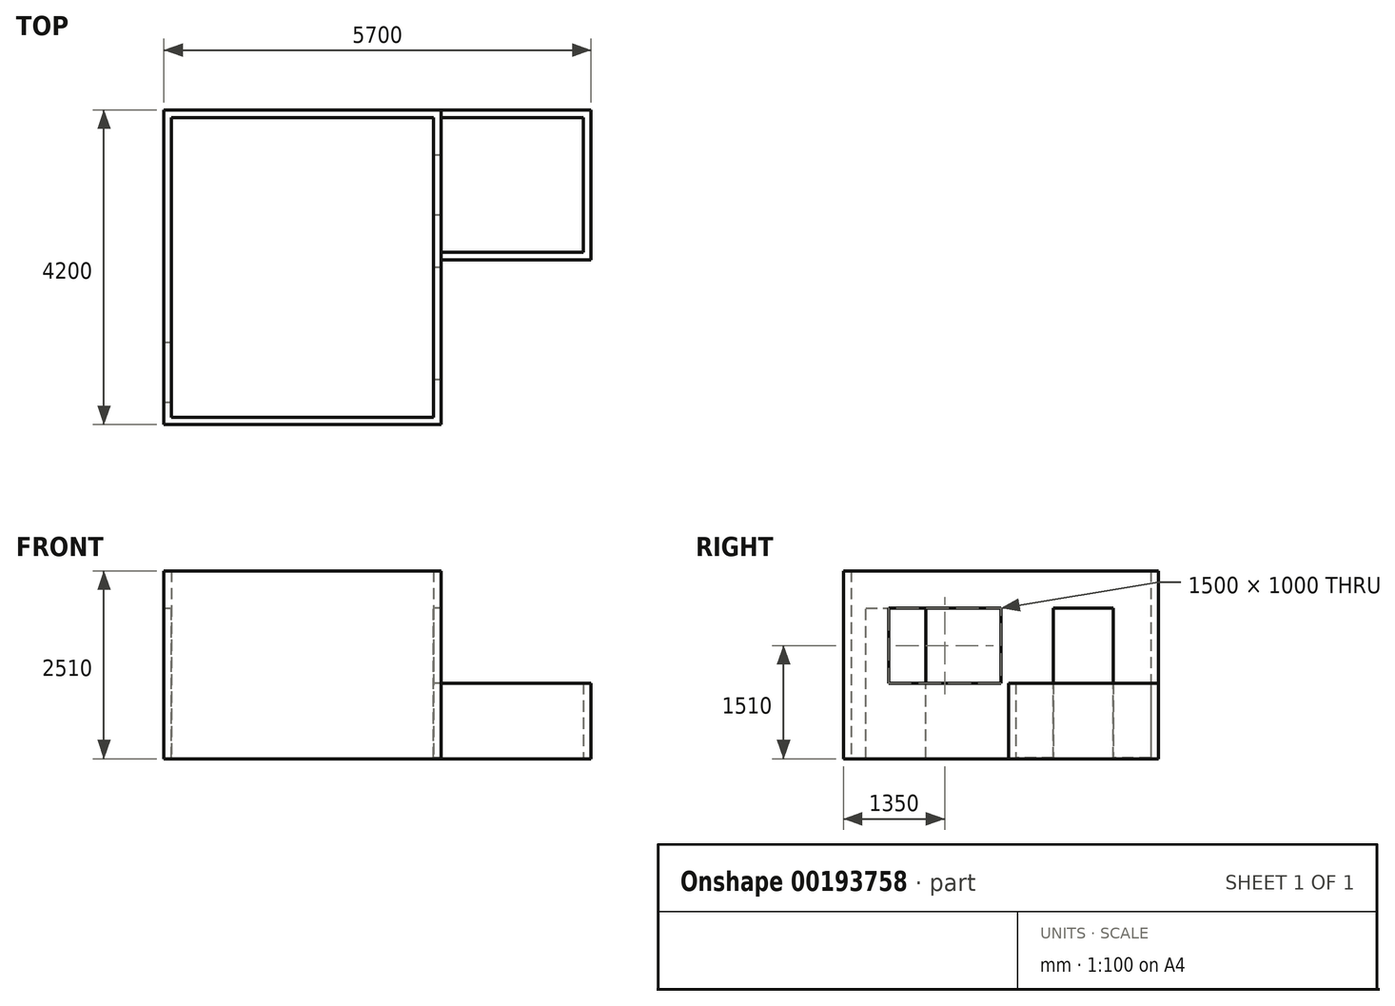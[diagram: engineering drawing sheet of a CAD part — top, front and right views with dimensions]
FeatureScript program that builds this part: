
annotation { "Feature Type Name" : "Feature", "Feature Type Description" : "" }
export const myFeature = defineFeature(function(context is Context, id is Id, definition is map)
    precondition{}
    {
        {
            var Q0;
            Q0=qCreatedBy(makeId("Top.planeOp"),FACE);
            var sketch = newSketch(context, id + "F0", { "sketchPlane" : qUnion([Q0])});
            skLineSegment(sketch, "E0.bottom", {"start": v(0, 0) * mm, "end": v(3500, 0) * mm, "construction": true});
            skLineSegment(sketch, "E0.top", {"start": v(0, 4000) * mm, "end": v(3500, 4000) * mm, "construction": true});
            skLineSegment(sketch, "E0.left", {"start": v(0, 0) * mm, "end": v(0, 4000) * mm, "construction": true});
            skLineSegment(sketch, "E0.right", {"start": v(3500, 0) * mm, "end": v(3500, 4000) * mm, "construction": true});
            skLineSegment(sketch, "E1.bottom", {"start": v(-100, 4100) * mm, "end": v(3600, 4100) * mm});
            skLineSegment(sketch, "E1.top", {"start": v(-100, -100) * mm, "end": v(3600, -100) * mm});
            skLineSegment(sketch, "E1.left", {"start": v(-100, 4100) * mm, "end": v(-100, -100) * mm});
            skLineSegment(sketch, "E1.right", {"start": v(3600, 4100) * mm, "end": v(3600, -100) * mm});
            skSolve(sketch);
        }
        {
            var Q0;
            Q0=makeQuery(id+"F0.imprint","IMPRINT",FACE,{"disambiguationData":[TD([[makeQuery(id+"F0.imprint","IMPRINT",EDGE,{"derivedFrom":sQuery(id+"F0.wireOp",EDGE,"E1.bottom")}),-1.0]])]});
            extrude(context, id + "F1", {"entities" : qUnion([Q0]), "oppositeDirection" : true, "depth" : 10 * mm});
        }
        {
            var Q0;
            Q0=makeQuery(id+"F0.imprint","IMPRINT",FACE,{"disambiguationData":[TD([[makeQuery(id+"F0.imprint","IMPRINT",EDGE,{"derivedFrom":sQuery(id+"F0.wireOp",EDGE,"E1.bottom")}),-1.0]])]});
            var sketch = newSketch(context, id + "F2", { "sketchPlane" : qUnion([Q0])});
            skLineSegment(sketch, "E2.bottom", {"start": v(0, 0) * mm, "end": v(3500, 0) * mm});
            skLineSegment(sketch, "E2.top", {"start": v(0, 4000) * mm, "end": v(3500, 4000) * mm});
            skLineSegment(sketch, "E2.left", {"start": v(0, 0) * mm, "end": v(0, 4000) * mm});
            skLineSegment(sketch, "E2.right", {"start": v(3500, 0) * mm, "end": v(3500, 4000) * mm});
            skLineSegment(sketch, "E3.bottom", {"start": v(-100, 4100) * mm, "end": v(3600, 4100) * mm});
            skLineSegment(sketch, "E3.top", {"start": v(-100, -100) * mm, "end": v(3600, -100) * mm});
            skLineSegment(sketch, "E3.left", {"start": v(-100, 4100) * mm, "end": v(-100, -100) * mm});
            skLineSegment(sketch, "E3.right", {"start": v(3600, 4100) * mm, "end": v(3600, -100) * mm});
            skSolve(sketch);
        }
        {
            var Q0;
            Q0 = qSketchRegion(id + "F2", true);
            extrude(context, id + "F3", {"entities" : qUnion([Q0]), "operationType" : NewBodyOperationType.ADD, "depth" : 2500 * mm});
        }
        {
            var Q0;
            Q0=makeQuery(id+"F3.opExtrude","SWEPT_FACE",FACE,{"disambiguationData":[OSD([sQuery(id+"F2.wireOp",EDGE,"E2.left")])]});
            var sketch = newSketch(context, id + "F4", { "sketchPlane" : qUnion([Q0])});
            skLineSegment(sketch, "E4.bottom", {"start": v(200, 0) * mm, "end": v(1000, 0) * mm});
            skLineSegment(sketch, "E4.top", {"start": v(200, 2000) * mm, "end": v(1000, 2000) * mm});
            skLineSegment(sketch, "E4.left", {"start": v(200, 0) * mm, "end": v(200, 2000) * mm});
            skLineSegment(sketch, "E4.right", {"start": v(1000, 0) * mm, "end": v(1000, 2000) * mm});
            skSolve(sketch);
        }
        {
            var Q0;
            Q0 = qSketchRegion(id + "F4", true);
            extrude(context, id + "F5", {"entities" : qUnion([Q0]), "operationType" : NewBodyOperationType.REMOVE, "endBound" : BoundingType.UP_TO_NEXT, "oppositeDirection" : true, "depth" : 25 * mm});
        }
        {
            var Q0;
            Q0=makeQuery(id+"F3.opExtrude","SWEPT_FACE",FACE,{"disambiguationData":[OSD([sQuery(id+"F2.wireOp",EDGE,"E2.right")])]});
            var sketch = newSketch(context, id + "F6", { "sketchPlane" : qUnion([Q0])});
            skLineSegment(sketch, "E5.bottom", {"start": v(-3500, 0) * mm, "end": v(-2700, 0) * mm});
            skLineSegment(sketch, "E5.top", {"start": v(-3500, 2000) * mm, "end": v(-2700, 2000) * mm});
            skLineSegment(sketch, "E5.left", {"start": v(-3500, 0) * mm, "end": v(-3500, 2000) * mm});
            skLineSegment(sketch, "E5.right", {"start": v(-2700, 0) * mm, "end": v(-2700, 2000) * mm});
            skSolve(sketch);
        }
        {
            var Q0;
            Q0 = qSketchRegion(id + "F6", true);
            extrude(context, id + "F7", {"entities" : qUnion([Q0]), "operationType" : NewBodyOperationType.REMOVE, "endBound" : BoundingType.UP_TO_NEXT, "oppositeDirection" : true, "depth" : 25 * mm});
        }
        {
            var Q0;
            Q0=makeQuery(id+"F1.opExtrude","CAP_FACE",FACE,{"disambiguationData":[OSD([sQuery(id+"F0.wireOp",EDGE,"E1.bottom"),sQuery(id+"F0.wireOp",EDGE,"E1.top"),sQuery(id+"F0.wireOp",EDGE,"E1.left"),sQuery(id+"F0.wireOp",EDGE,"E1.right")])],"isStart":false});
            var sketch = newSketch(context, id + "F8", { "sketchPlane" : qUnion([Q0])});
            skLineSegment(sketch, "E6.bottom", {"start": v(3600, -4100) * mm, "end": v(5600, -4100) * mm});
            skLineSegment(sketch, "E6.top", {"start": v(3600, -2100) * mm, "end": v(5600, -2100) * mm});
            skLineSegment(sketch, "E6.left", {"start": v(3600, -4100) * mm, "end": v(3600, -2100) * mm});
            skLineSegment(sketch, "E6.right", {"start": v(5600, -4100) * mm, "end": v(5600, -2100) * mm});
            skSolve(sketch);
        }
        {
            var Q0;
            Q0 = qSketchRegion(id + "F8", true);
            var Q1;
            Q1=makeQuery(id+"F7.boolean.opBoolean","MERGE",FACE,{"derivedFrom":[makeQuery(id+"F5.boolean.opBoolean","MERGE",FACE,{"derivedFrom":[makeQuery(id+"F1.opExtrude","CAP_FACE",FACE,{"disambiguationData":[OSD([sQuery(id+"F0.wireOp",EDGE,"E1.bottom"),sQuery(id+"F0.wireOp",EDGE,"E1.top"),sQuery(id+"F0.wireOp",EDGE,"E1.left"),sQuery(id+"F0.wireOp",EDGE,"E1.right")])],"isStart":true}),makeQuery(id+"F5.opExtrude","SWEPT_FACE",FACE,{"disambiguationData":[OSD([sQuery(id+"F4.wireOp",EDGE,"E4.bottom")])]})]}),makeQuery(id+"F7.opExtrude","SWEPT_FACE",FACE,{"disambiguationData":[OSD([sQuery(id+"F6.wireOp",EDGE,"E5.bottom")])]})]});
            extrude(context, id + "F9", {"entities" : qUnion([Q0]), "operationType" : NewBodyOperationType.ADD, "endBound" : BoundingType.UP_TO_SURFACE, "oppositeDirection" : true, "endBoundEntityFace" : qUnion([Q1]), "depth" : 25 * mm});
        }
        {
            var Q0;
            {var subQ0=sQuery(id+"F6.wireOp",EDGE,"E5.bottom");var subQ1=sQuery(id+"F4.wireOp",EDGE,"E4.bottom");var subQ2=sQuery(id+"F0.wireOp",EDGE,"E1.right");var subQ3=sQuery(id+"F0.wireOp",EDGE,"E1.left");var subQ4=sQuery(id+"F0.wireOp",EDGE,"E1.top");var subQ5=sQuery(id+"F0.wireOp",EDGE,"E1.bottom");Q0=makeQuery(id+"F9.boolean.opBoolean","MERGE",FACE,{"derivedFrom":[makeQuery(id+"F7.boolean.opBoolean","MERGE",FACE,{"derivedFrom":[makeQuery(id+"F5.boolean.opBoolean","MERGE",FACE,{"derivedFrom":[makeQuery(id+"F1.opExtrude","CAP_FACE",FACE,{"disambiguationData":[OSD([subQ5,subQ4,subQ3,subQ2])],"isStart":true}),makeQuery(id+"F5.opExtrude","SWEPT_FACE",FACE,{"disambiguationData":[OSD([subQ1])]})]}),makeQuery(id+"F7.opExtrude","SWEPT_FACE",FACE,{"disambiguationData":[OSD([subQ0])]})]}),makeQuery(id+"F9.opExtrude","CAP_FACE",FACE,{"disambiguationData":[OSD([subQ5,subQ4,subQ3,subQ2,subQ1,subQ0])],"isStart":false})]});}
            var sketch = newSketch(context, id + "F10", { "sketchPlane" : qUnion([Q0])});
            skLineSegment(sketch, "E7", {"start": v(3600, 4100) * mm, "end": v(5600, 4100) * mm});
            skLineSegment(sketch, "E8", {"start": v(5600, 4100) * mm, "end": v(5600, 2100) * mm});
            skLineSegment(sketch, "E9", {"start": v(5600, 2100) * mm, "end": v(3600, 2100) * mm});
            skLineSegment(sketch, "E10", {"start": v(3600, 2100) * mm, "end": v(3600, 2200) * mm});
            skLineSegment(sketch, "E11", {"start": v(3600, 2200) * mm, "end": v(5500, 2200) * mm});
            skLineSegment(sketch, "E12", {"start": v(5500, 2200) * mm, "end": v(5500, 4000) * mm});
            skLineSegment(sketch, "E13", {"start": v(5500, 4000) * mm, "end": v(3600, 4000) * mm});
            skLineSegment(sketch, "E14", {"start": v(3600, 4000) * mm, "end": v(3600, 4100) * mm});
            skSolve(sketch);
        }
        {
            var Q0;
            Q0 = qSketchRegion(id + "F10", true);
            extrude(context, id + "F11", {"entities" : qUnion([Q0]), "operationType" : NewBodyOperationType.ADD, "depth" : 1000 * mm});
        }
        {
            var Q0;
            Q0=makeQuery(id+"F3.opExtrude","SWEPT_FACE",FACE,{"disambiguationData":[OSD([sQuery(id+"F2.wireOp",EDGE,"E2.right")])]});
            var sketch = newSketch(context, id + "F12", { "sketchPlane" : qUnion([Q0])});
            skLineSegment(sketch, "E15.bottom", {"start": v(-2000, 2000) * mm, "end": v(-500, 2000) * mm});
            skLineSegment(sketch, "E15.top", {"start": v(-2000, 1000) * mm, "end": v(-500, 1000) * mm});
            skLineSegment(sketch, "E15.left", {"start": v(-2000, 2000) * mm, "end": v(-2000, 1000) * mm});
            skLineSegment(sketch, "E15.right", {"start": v(-500, 2000) * mm, "end": v(-500, 1000) * mm});
            skSolve(sketch);
        }
        {
            var Q0;
            Q0=makeQuery(id+"F12.imprint","IMPRINT",FACE,{"disambiguationData":[TD([[makeQuery(id+"F12.imprint","IMPRINT",EDGE,{"derivedFrom":sQuery(id+"F12.wireOp",EDGE,"E15.bottom")}),-1.0]])]});
            extrude(context, id + "F13", {"entities" : qUnion([Q0]), "operationType" : NewBodyOperationType.REMOVE, "endBound" : BoundingType.UP_TO_NEXT, "oppositeDirection" : true, "depth" : 25 * mm});
        }
    });
